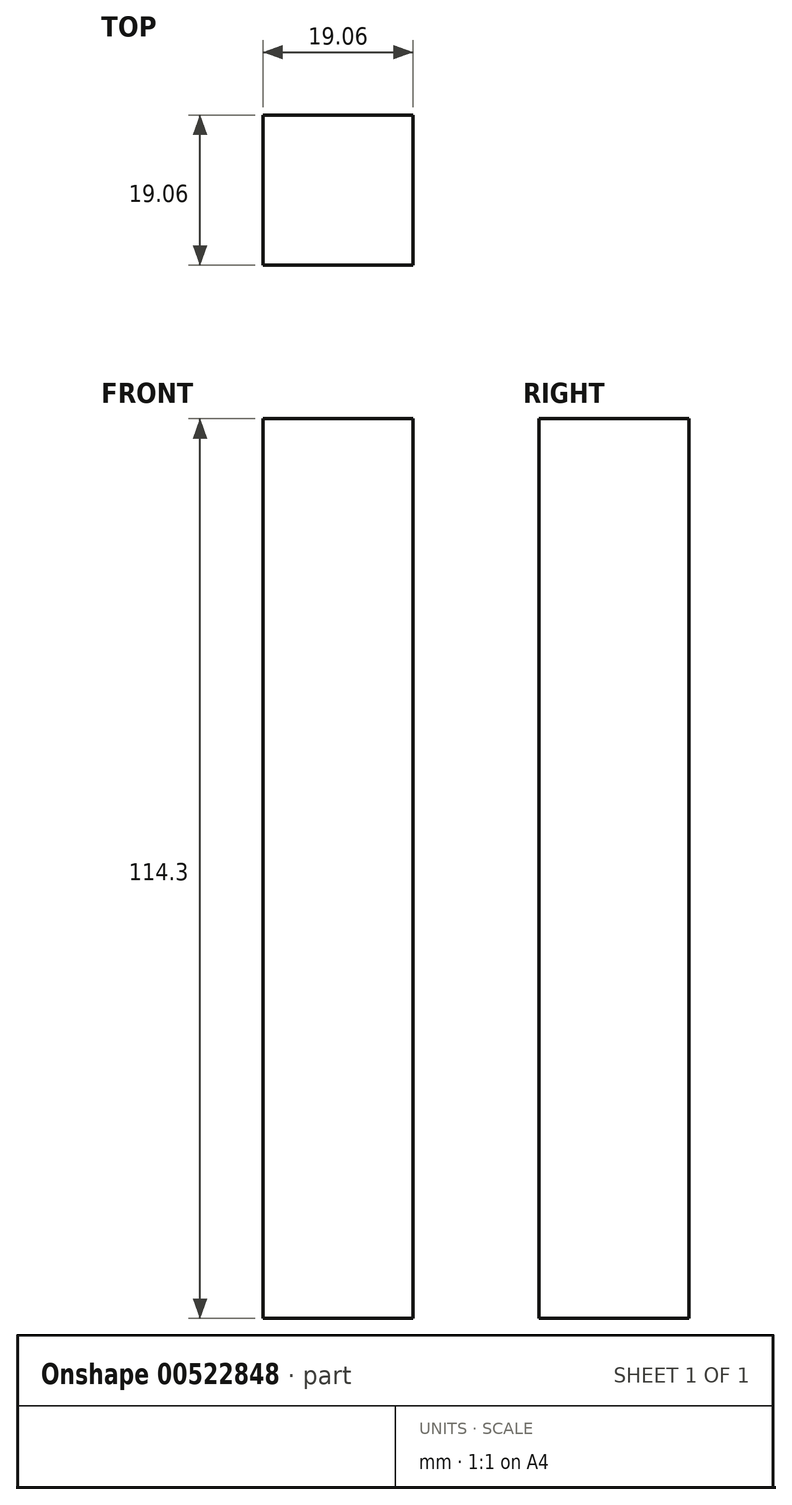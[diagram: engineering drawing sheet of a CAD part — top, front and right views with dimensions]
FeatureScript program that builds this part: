
annotation { "Feature Type Name" : "Feature", "Feature Type Description" : "" }
export const myFeature = defineFeature(function(context is Context, id is Id, definition is map)
    precondition{}
    {
        {
            var Q0;
            Q0=qCreatedBy(makeId("Top.planeOp"),FACE);
            var sketch = newSketch(context, id + "F0", { "sketchPlane" : qUnion([Q0])});
            skLineSegment(sketch, "E0.bottom", {"start": v(-9.52, 9.52) * mm, "end": v(9.53, 9.52) * mm});
            skLineSegment(sketch, "E0.top", {"start": v(-9.53, -9.53) * mm, "end": v(9.53, -9.53) * mm});
            skLineSegment(sketch, "E0.left", {"start": v(-9.53, 9.52) * mm, "end": v(-9.53, -9.53) * mm});
            skLineSegment(sketch, "E0.right", {"start": v(9.53, 9.52) * mm, "end": v(9.53, -9.53) * mm});
            skPoint(sketch, "E0.middle", {"position": v(0, 0) * mm});
            skSolve(sketch);
        }
        {
            var Q0;
            Q0=makeQuery(id+"F0.imprint","IMPRINT",FACE,{"disambiguationData":[TD([[makeQuery(id+"F0.imprint","IMPRINT",EDGE,{"derivedFrom":sQuery(id+"F0.wireOp",EDGE,"E0.bottom")}),-1.0]])]});
            extrude(context, id + "F1", {"entities" : qUnion([Q0]), "depth" : 114.3 * mm, "offsetDistance" : 25.4 * mm});
        }
    });
